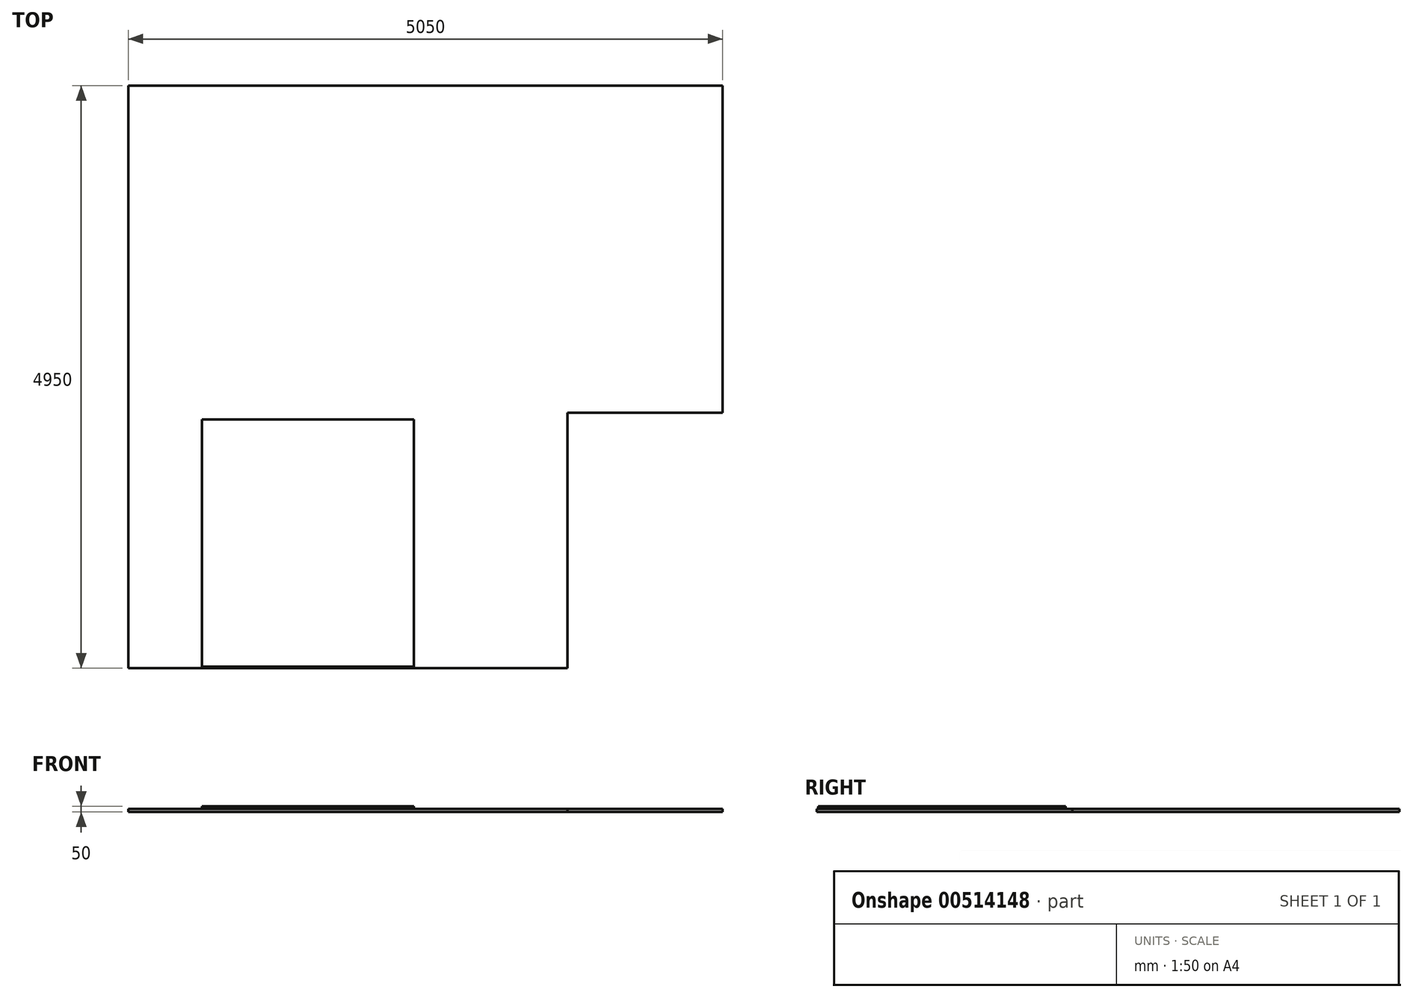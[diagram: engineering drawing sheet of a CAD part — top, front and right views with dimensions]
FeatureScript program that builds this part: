
annotation { "Feature Type Name" : "Feature", "Feature Type Description" : "" }
export const myFeature = defineFeature(function(context is Context, id is Id, definition is map)
    precondition{}
    {
        {
            var Q0;
            Q0=qCreatedBy(makeId("Top.planeOp"),FACE);
            var sketch = newSketch(context, id + "F0", { "sketchPlane" : qUnion([Q0])});
            skLineSegment(sketch, "E0", {"start": v(2519.17, 2925.7) * mm, "end": v(-2530.83, 2925.7) * mm});
            skLineSegment(sketch, "E1", {"start": v(-2530.83, 2925.7) * mm, "end": v(-2530.83, -2024.3) * mm});
            skLineSegment(sketch, "E2", {"start": v(-2530.83, -2024.3) * mm, "end": v(1199.17, -2024.3) * mm});
            skLineSegment(sketch, "E3", {"start": v(1199.17, -2024.3) * mm, "end": v(1199.17, 145.7) * mm});
            skLineSegment(sketch, "E4", {"start": v(1199.17, 145.7) * mm, "end": v(2519.17, 145.7) * mm});
            skLineSegment(sketch, "E5", {"start": v(2519.17, 145.7) * mm, "end": v(2519.17, 2925.7) * mm});
            skSolve(sketch);
        }
        {
            var Q0;
            Q0=makeQuery(id+"F0.imprint","IMPRINT",FACE,{"disambiguationData":[TD([[makeQuery(id+"F0.imprint","IMPRINT",EDGE,{"derivedFrom":sQuery(id+"F0.wireOp",EDGE,"E0")}),1.0]])]});
            extrude(context, id + "F1", {"entities" : qUnion([Q0]), "depth" : 25 * mm});
        }
        {
            var Q0;
            Q0=makeQuery(id+"F1.opExtrude","CAP_FACE",FACE,{"disambiguationData":[OSD([sQuery(id+"F0.wireOp",EDGE,"E0"),sQuery(id+"F0.wireOp",EDGE,"E1"),sQuery(id+"F0.wireOp",EDGE,"E2"),sQuery(id+"F0.wireOp",EDGE,"E3"),sQuery(id+"F0.wireOp",EDGE,"E4"),sQuery(id+"F0.wireOp",EDGE,"E5")])],"isStart":false});
            var sketch = newSketch(context, id + "F2", { "sketchPlane" : qUnion([Q0])});
            skLineSegment(sketch, "E6.bottom", {"start": v(-2913.88, 1787.93) * mm, "end": v(-1113.88, 1787.93) * mm});
            skLineSegment(sketch, "E6.top", {"start": v(-2913.88, -312.07) * mm, "end": v(-1113.88, -312.07) * mm});
            skLineSegment(sketch, "E6.left", {"start": v(-2913.88, 1787.93) * mm, "end": v(-2913.88, -312.07) * mm});
            skLineSegment(sketch, "E6.right", {"start": v(-1113.88, 1787.93) * mm, "end": v(-1113.88, -312.07) * mm});
            skSolve(sketch);
        }
        {
            var Q0;
            {var subQ0=sQuery(id+"F2.wireOp",EDGE,"E6.right");Q0=makeQuery(id+"F2.imprint","IMPRINT",FACE,{"disambiguationData":[TD([[makeQuery(id+"F2.imprint","IMPRINT",EDGE,{"derivedFrom":subQ0}),-1.0]])]});}
            var Q1;
            {var subQ0=sQuery(id+"F2.wireOp",EDGE,"E6.left");Q1=makeQuery(id+"F2.imprint","IMPRINT",FACE,{"disambiguationData":[TD([[makeQuery(id+"F2.imprint","IMPRINT",EDGE,{"derivedFrom":subQ0}),1.0]])]});}
            extrude(context, id + "F3", {"entities" : qUnion([Q0, Q1]), "depth" : 25 * mm});
        }
        {
            var Q0;
            Q0=makeQuery(id+"F3.opExtrude","SWEPT_BODY",BODY,{"disambiguationData":[OSD([sQuery(id+"F2.wireOp",EDGE,"E6.bottom"),sQuery(id+"F2.wireOp",EDGE,"E6.top"),sQuery(id+"F2.wireOp",EDGE,"E6.left"),sQuery(id+"F2.wireOp",EDGE,"E6.right")])]});
            transform(context, id + "F4", {"entities" : qUnion([Q0]), "transformType" : TransformType.TRANSLATION_3D, "dx" : 1010 * mm, "dy" : -1700 * mm, "dz" : 0 * mm, "makeCopy" : false});
        }
    });
